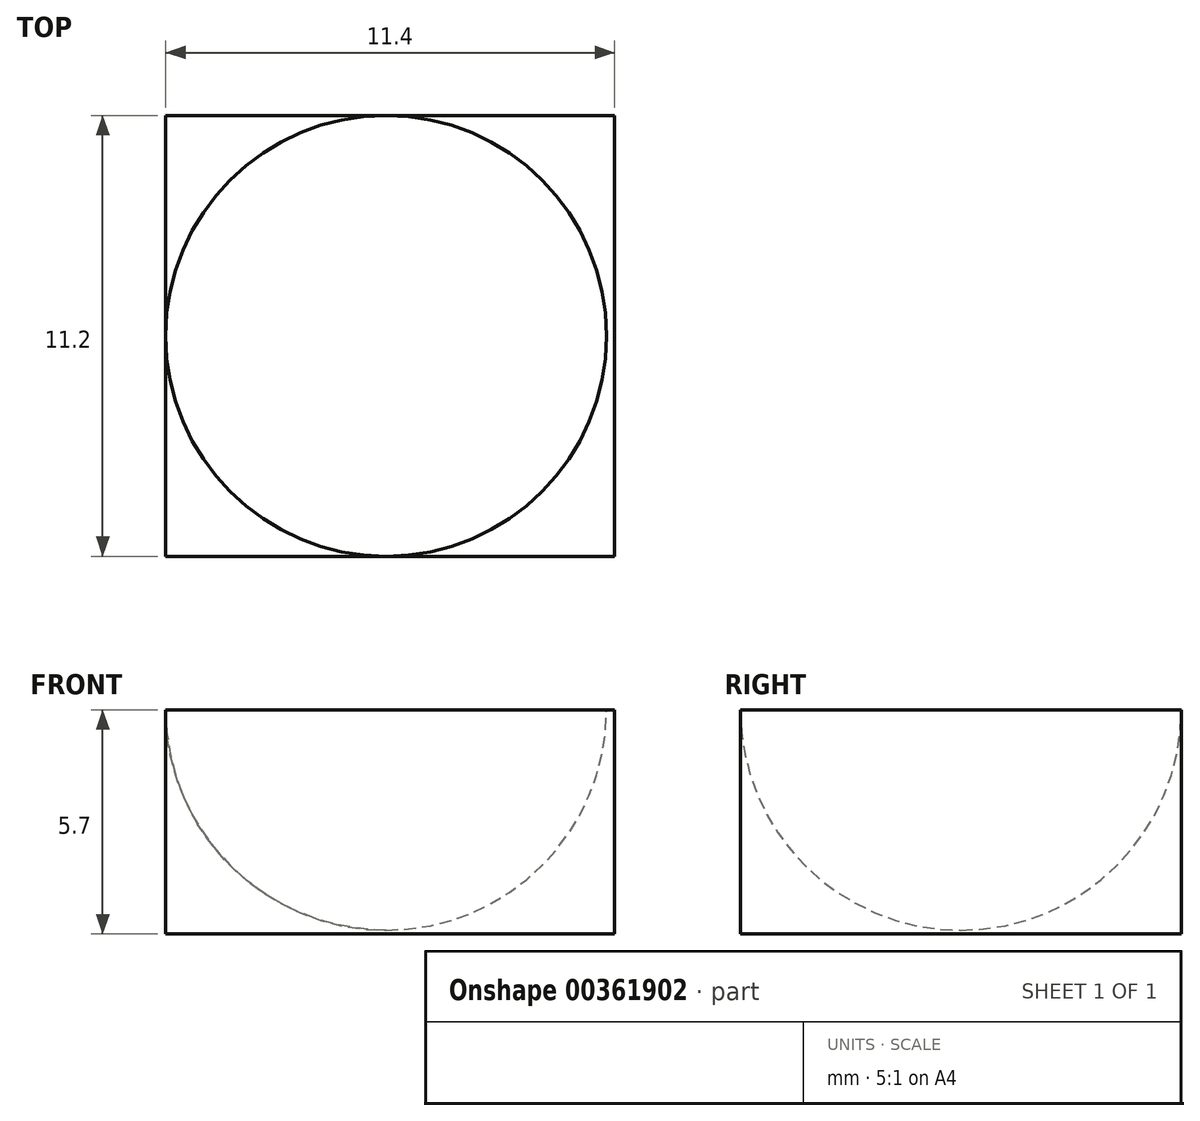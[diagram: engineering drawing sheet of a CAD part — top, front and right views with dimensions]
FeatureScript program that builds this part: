
annotation { "Feature Type Name" : "Feature", "Feature Type Description" : "" }
export const myFeature = defineFeature(function(context is Context, id is Id, definition is map)
    precondition{}
    {
        {
            var Q0;
            Q0=qCreatedBy(makeId("Front.planeOp"),FACE);
            var sketch = newSketch(context, id + "F0", { "sketchPlane" : qUnion([Q0])});
            skLineSegment(sketch, "E0.bottom", {"start": v(5.8, -5.7) * mm, "end": v(-5.6, -5.7) * mm});
            skLineSegment(sketch, "E0.top", {"start": v(5.8, 0) * mm, "end": v(-5.6, 0) * mm});
            skLineSegment(sketch, "E0.left", {"start": v(5.8, -5.7) * mm, "end": v(5.8, 0) * mm});
            skLineSegment(sketch, "E0.right", {"start": v(-5.6, -5.7) * mm, "end": v(-5.6, 0) * mm});
            skPoint(sketch, "E0.middle", {"position": v(0.1, -2.85) * mm});
            skSolve(sketch);
        }
        {
            var Q0;
            Q0 = qSketchRegion(id + "F0", true);
            extrude(context, id + "F1", {"entities" : qUnion([Q0]), "endBound" : BoundingType.SYMMETRIC, "depth" : 11.2 * mm});
        }
        {
            var Q0;
            Q0=qCreatedBy(makeId("Front.planeOp"),FACE);
            var sketch = newSketch(context, id + "F2", { "sketchPlane" : qUnion([Q0])});
            skLineSegment(sketch, "E1", {"start": v(0, 5.6) * mm, "end": v(0, -5.6) * mm});
            skArc(sketch, "E2", {"start": v(0, -5.6) * mm, "mid": v(5.6, 0) * mm, "end": v(0, 5.6) * mm});
            skSolve(sketch);
        }
        {
            var Q0;
            Q0 = qSketchRegion(id + "F2", true);
            var Q1;
            Q1=sQuery(id+"F2.wireOp",EDGE,"E1");
            revolve(context, id + "F3", {"operationType" : NewBodyOperationType.REMOVE, "entities" : qUnion([Q0]), "axis" : qUnion([Q1]), "revolveType" : RevolveType.FULL});
        }
    });
